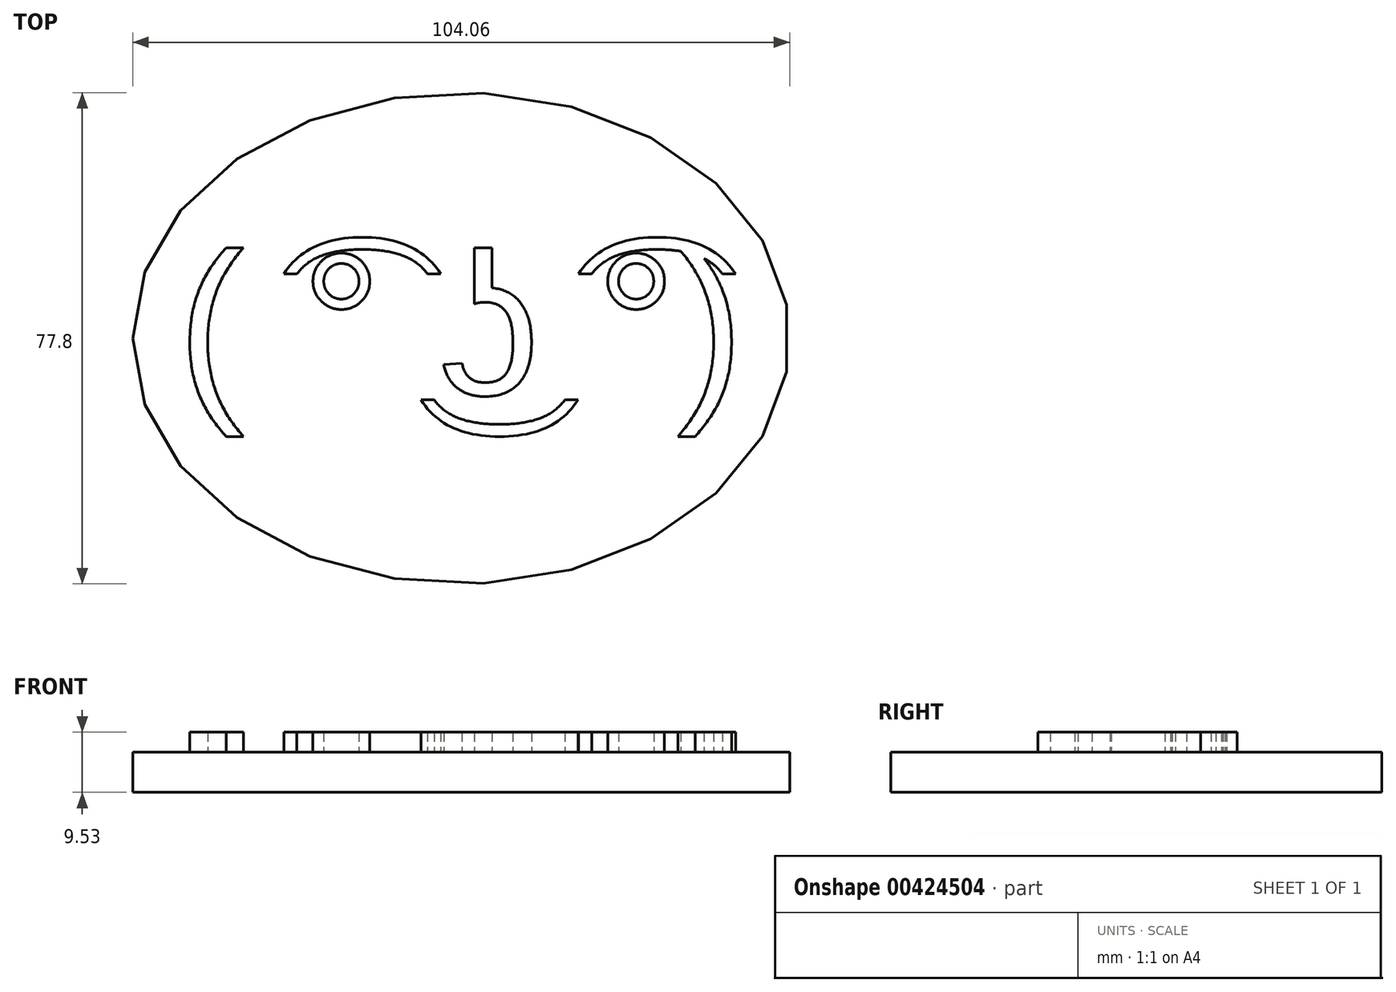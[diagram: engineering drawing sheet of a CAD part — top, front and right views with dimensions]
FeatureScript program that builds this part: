
annotation { "Feature Type Name" : "Feature", "Feature Type Description" : "" }
export const myFeature = defineFeature(function(context is Context, id is Id, definition is map)
    precondition{}
    {
        {
            var Q0;
            Q0=qCreatedBy(makeId("Top.planeOp"),FACE);
            var sketch = newSketch(context, id + "F0", { "sketchPlane" : qUnion([Q0])});
            skEllipse(sketch, "E0", {"center": v(0, 0) * mm, "majorRadius": 52.03 * mm, "minorRadius": 38.9 * mm, "majorAxis": v(-1, 0)});
            skSolve(sketch);
        }
        {
            var Q0;
            Q0=makeQuery(id+"F0.imprint","IMPRINT",FACE,{"disambiguationData":[TD([[makeQuery(id+"F0.imprint","IMPRINT",EDGE,{"derivedFrom":sQuery(id+"F0.wireOp",EDGE,"E0")}),1.0]])]});
            extrude(context, id + "F1", {"entities" : qUnion([Q0]), "depth" : 6.35 * mm});
        }
        {
            var Q0;
            Q0=makeQuery(id+"F1.opExtrude","CAP_FACE",FACE,{"disambiguationData":[OSD([sQuery(id+"F0.wireOp",EDGE,"E0")])],"isStart":false});
            var sketch = newSketch(context, id + "F2", { "sketchPlane" : qUnion([Q0])});
            skText(sketch, "E1", { "text": "( ͡° ͜ʖ ͡°)", "fontName": "Arimo-Regular.ttf"});
            const initialGuessF2  = {"E1": [-0.045, -0.00891, 1, 0, 0.0231]};
            skSetInitialGuess(sketch, initialGuessF2);
            skSolve(sketch);
        }
        {
            var Q0;
            Q0 = qSketchRegion(id + "F2", true);
            extrude(context, id + "F3", {"entities" : qUnion([Q0]), "operationType" : NewBodyOperationType.ADD, "depth" : 3.17 * mm});
        }
    });
